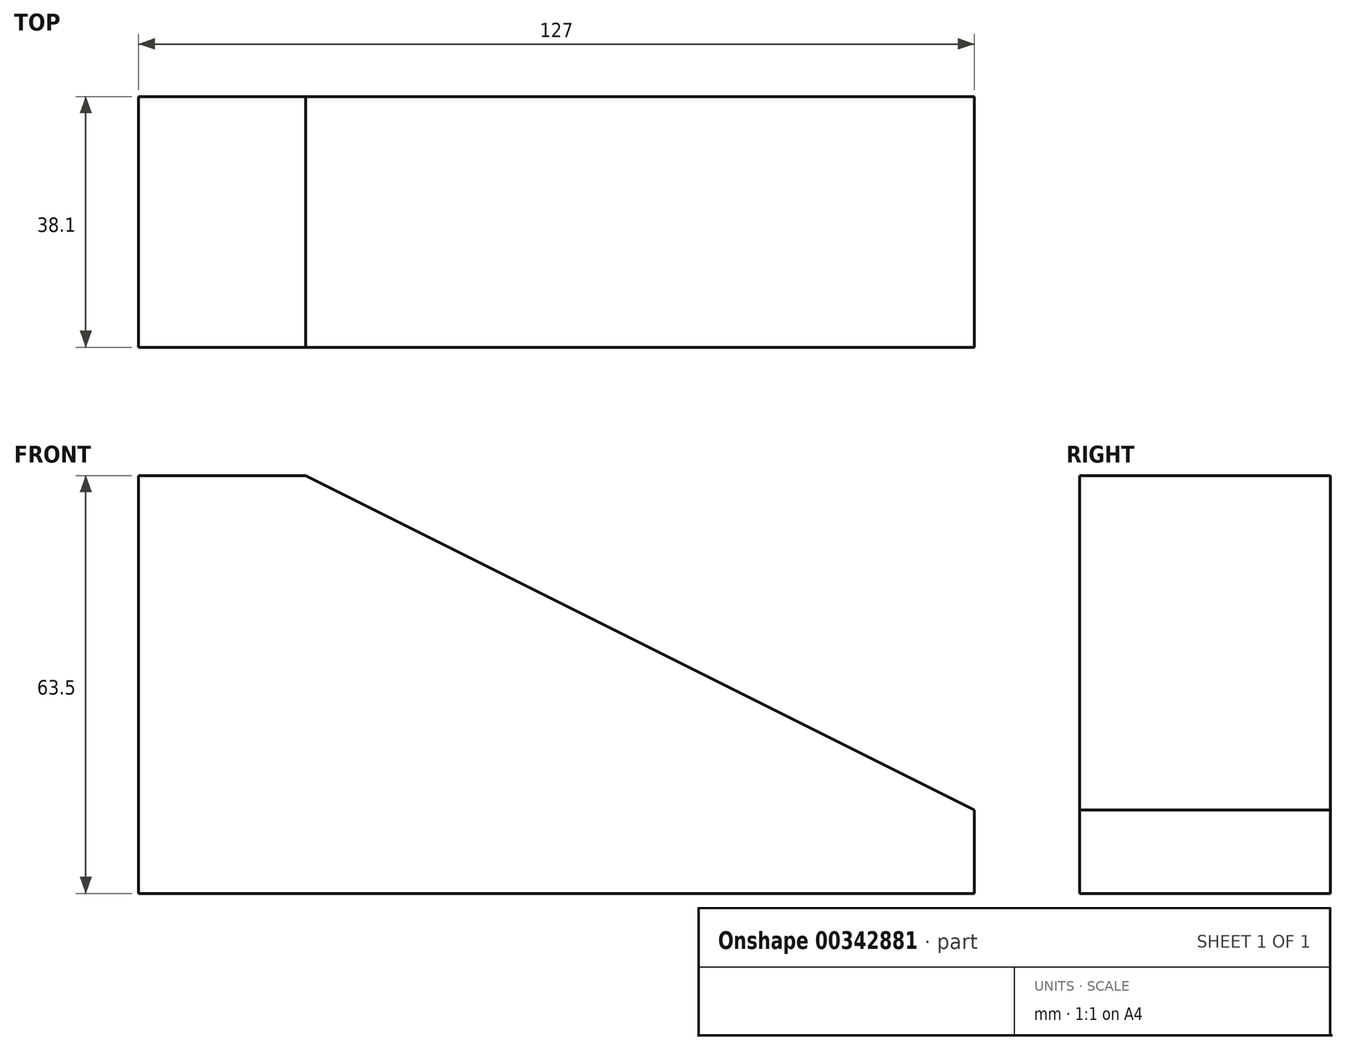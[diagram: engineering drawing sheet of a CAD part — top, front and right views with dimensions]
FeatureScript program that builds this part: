
annotation { "Feature Type Name" : "Feature", "Feature Type Description" : "" }
export const myFeature = defineFeature(function(context is Context, id is Id, definition is map)
    precondition{}
    {
        {
            var Q0;
            Q0=qCreatedBy(makeId("Front.planeOp"),FACE);
            var sketch = newSketch(context, id + "F0", { "sketchPlane" : qUnion([Q0])});
            skLineSegment(sketch, "E0.bottom", {"start": v(-127, 0) * mm, "end": v(0, 0) * mm});
            skLineSegment(sketch, "E0.top", {"start": v(-127, 63.5) * mm, "end": v(-101.6, 63.5) * mm});
            skLineSegment(sketch, "E0.left", {"start": v(-127, 0) * mm, "end": v(-127, 63.5) * mm});
            skLineSegment(sketch, "E0.right", {"start": v(0, 0) * mm, "end": v(0, 12.7) * mm});
            skLineSegment(sketch, "E1.top", {"start": v(-127, 0) * mm, "end": v(-101.6, 0) * mm});
            skLineSegment(sketch, "E1.left", {"start": v(-127, 63.5) * mm, "end": v(-127, 0) * mm});
            skLineSegment(sketch, "E1.right", {"start": v(-101.6, 63.5) * mm, "end": v(-101.6, 0) * mm});
            skLineSegment(sketch, "E2.top", {"start": v(0, 0) * mm, "end": v(-29.96, 0) * mm});
            skLineSegment(sketch, "E2.left", {"start": v(0, 12.7) * mm, "end": v(0, 0) * mm});
            skLineSegment(sketch, "E3", {"start": v(-101.6, 63.5) * mm, "end": v(0, 12.7) * mm});
            skPoint(sketch, "E4.orphan", {"position": v(0, 63.5) * mm});
            skSolve(sketch);
        }
        {
            var Q0;
            Q0=makeQuery(id+"F0.imprint","IMPRINT",FACE,{"disambiguationData":[TD([[makeQuery(id+"F0.imprint","IMPRINT",EDGE,{"derivedFrom":sQuery(id+"F0.wireOp",EDGE,"E2.bottom")}),1.0]])]});
            var Q1;
            Q1=makeQuery(id+"F0.imprint","IMPRINT",FACE,{"disambiguationData":[TD([[makeQuery(id+"F0.imprint","IMPRINT",EDGE,{"derivedFrom":sQuery(id+"F0.wireOp",EDGE,"E0.bottom")}),1.0]])]});
            var Q2;
            Q2=makeQuery(id+"F0.imprint","IMPRINT",FACE,{"disambiguationData":[TD([[makeQuery(id+"F0.imprint","IMPRINT",EDGE,{"derivedFrom":sQuery(id+"F0.wireOp",EDGE,"E0.top")}),-1.0]])]});
            extrude(context, id + "F1", {"entities" : qUnion([Q0, Q1, Q2]), "depth" : 38.1 * mm});
        }
    });
